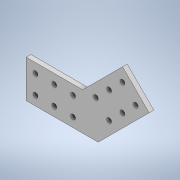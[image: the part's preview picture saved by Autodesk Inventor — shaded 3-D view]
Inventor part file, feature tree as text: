
AUTODESK INVENTOR PART (.ipt)
format: ipt  version: 2020 (Build 240168000, 168)  size: 132,608 bytes
history: native  units: in
note: dims shown in document units (in); Inventor stores cm internally (conversion verified against a paired STEP export)
features: extrude x1, sketch x1
ambient origin geometry x8: Origin, YZ Plane, XZ Plane, XY Plane, X Axis, Y Axis, Z Axis, Center Point
bodies: Solid1 (feature_tree)
feature tree (2):
  extrude  "Extrusion1"  Depth=0.25in
  sketch  "Sketch1"  dims[d0=2.0in d1=3.0in d2=3.0in d3=135.0deg d4=2.0in d5=0.256in d6=0.5in d7=0.5in d8=0.7874in d10=1.0in d11=1.1811in d13=1.0in d16=0.256in d17=0.5in d18=0.5in d19=1.1811in d21=1.0in d22=0.7874in d24=1.0in d27=0.25in d28=0.0in]
